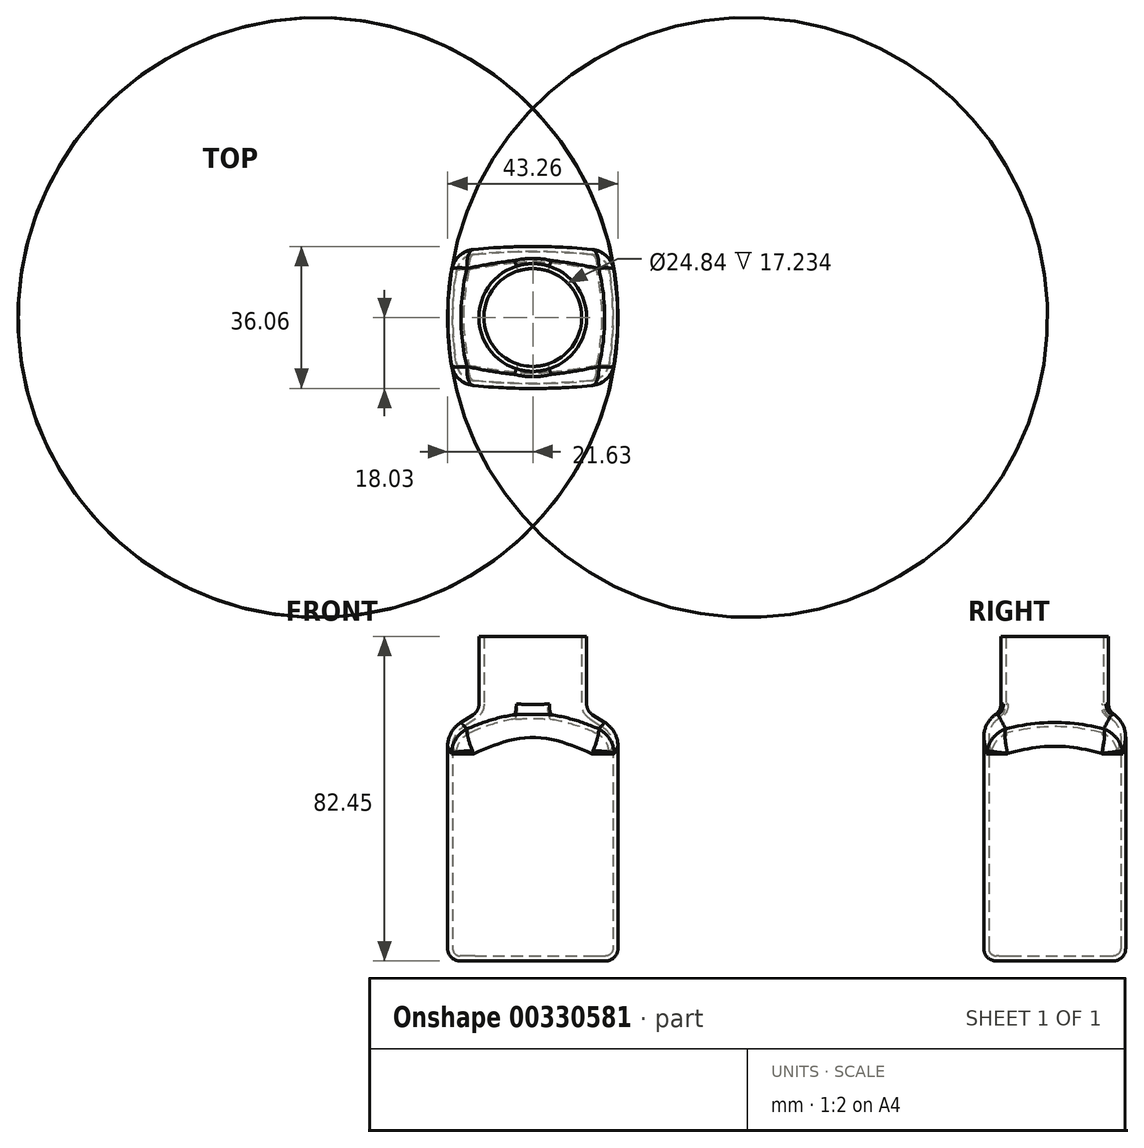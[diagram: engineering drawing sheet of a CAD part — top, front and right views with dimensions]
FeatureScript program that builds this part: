
annotation { "Feature Type Name" : "Feature", "Feature Type Description" : "" }
export const myFeature = defineFeature(function(context is Context, id is Id, definition is map)
    precondition{}
    {
        {
            var Q0;
            Q0=qCreatedBy(makeId("Top.planeOp"),FACE);
            var sketch = newSketch(context, id + "F0", { "sketchPlane" : qUnion([Q0])});
            skLineSegment(sketch, "E0.bottom", {"start": v(21.63, -18.03) * mm, "end": v(-21.63, -18.03) * mm, "construction": true});
            skLineSegment(sketch, "E0.top", {"start": v(21.63, 18.03) * mm, "end": v(-21.63, 18.03) * mm, "construction": true});
            skLineSegment(sketch, "E0.left", {"start": v(21.63, -18.03) * mm, "end": v(21.63, 18.03) * mm, "construction": true});
            skLineSegment(sketch, "E0.right", {"start": v(-21.63, -18.03) * mm, "end": v(-21.63, 18.03) * mm, "construction": true});
            skPoint(sketch, "E0.middle", {"position": v(0, 0) * mm});
            skLineSegment(sketch, "E1.0", {"start": v(21.63, -134.37) * mm, "end": v(-21.63, -134.37) * mm, "construction": true});
            skLineSegment(sketch, "E2.0", {"start": v(21.63, 134.37) * mm, "end": v(-21.63, 134.37) * mm, "construction": true});
            skLineSegment(sketch, "E3.0", {"start": v(-54.57, -18.03) * mm, "end": v(-54.57, 18.03) * mm, "construction": true});
            skLineSegment(sketch, "E4.0", {"start": v(54.57, -18.03) * mm, "end": v(54.57, 18.03) * mm, "construction": true});
            skArc(sketch, "E5", {"start": v(-15.04, -17.3) * mm, "mid": v(0, -18.03) * mm, "end": v(15.04, -17.3) * mm});
            skArc(sketch, "E6", {"start": v(20.68, -11.97) * mm, "mid": v(21.63, 0) * mm, "end": v(20.68, 11.97) * mm});
            skArc(sketch, "E7", {"start": v(-20.68, 11.97) * mm, "mid": v(-21.63, 0) * mm, "end": v(-20.68, -11.97) * mm});
            skArc(sketch, "E8.trimOffspring", {"start": v(15.04, 17.3) * mm, "mid": v(0, 18.03) * mm, "end": v(-15.04, 17.3) * mm});
            skPoint(sketch, "E9.visualSharp", {"position": v(-19.77, 16.75) * mm});
            skArc(sketch, "E9.filletArc", {"start": v(-15.04, 17.3) * mm, "mid": v(-18.77, 15.6) * mm, "end": v(-20.68, 11.97) * mm});
            skPoint(sketch, "E10.visualSharp", {"position": v(-19.77, -16.75) * mm});
            skArc(sketch, "E10.filletArc", {"start": v(-20.68, -11.97) * mm, "mid": v(-18.77, -15.6) * mm, "end": v(-15.04, -17.3) * mm});
            skPoint(sketch, "E11.visualSharp", {"position": v(19.77, -16.75) * mm});
            skArc(sketch, "E11.filletArc", {"start": v(15.04, -17.3) * mm, "mid": v(18.77, -15.6) * mm, "end": v(20.68, -11.97) * mm});
            skPoint(sketch, "E12.visualSharp", {"position": v(19.77, 16.75) * mm});
            skArc(sketch, "E12.filletArc", {"start": v(20.68, 11.97) * mm, "mid": v(18.77, 15.6) * mm, "end": v(15.04, 17.3) * mm});
            skSolve(sketch);
        }
        {
            var Q0;
            Q0 = qSketchRegion(id + "F0", true);
            extrude(context, id + "F1", {"entities" : qUnion([Q0]), "depth" : 82.45 * mm});
        }
        {
            var Q0;
            Q0=qCreatedBy(makeId("Front.planeOp"),FACE);
            var sketch = newSketch(context, id + "F2", { "sketchPlane" : qUnion([Q0])});
            skLineSegment(sketch, "E13", {"start": v(0, 0) * mm, "end": v(0, 82.45) * mm, "construction": true});
            skLineSegment(sketch, "E14.0", {"start": v(13.7, 63.48) * mm, "end": v(13.7, 82.45) * mm});
            skLineSegment(sketch, "E15", {"start": v(0, 82.45) * mm, "end": v(13.7, 82.45) * mm, "construction": true});
            skLineSegment(sketch, "E16", {"start": v(0, 0) * mm, "end": v(21.63, 0) * mm, "construction": true});
            skLineSegment(sketch, "E17.0", {"start": v(0, 54.56) * mm, "end": v(21.63, 54.56) * mm, "construction": true});
            skLineSegment(sketch, "E18", {"start": v(21.63, 0) * mm, "end": v(21.63, 54.56) * mm, "construction": true});
            skArc(sketch, "E19", {"start": v(21.63, 54.56) * mm, "mid": v(20.73, 58.02) * mm, "end": v(18.27, 60.61) * mm, "construction": true});
            skLineSegment(sketch, "E20", {"start": v(34.01, 50.78) * mm, "end": v(13.7, 63.48) * mm});
            skLineSegment(sketch, "E21", {"start": v(34.01, 82.45) * mm, "end": v(13.7, 82.45) * mm});
            skLineSegment(sketch, "E22", {"start": v(34.01, 50.78) * mm, "end": v(34.01, 82.45) * mm});
            skSolve(sketch);
        }
        {
            var Q0;
            Q0=makeQuery(id+"F2.imprint","IMPRINT",FACE,{"disambiguationData":[TD([[makeQuery(id+"F2.imprint","IMPRINT",EDGE,{"derivedFrom":sQuery(id+"F2.wireOp",EDGE,"E14.0")}),-1.0]])]});
            var Q1;
            Q1=sQuery(id+"F2.wireOp",EDGE,"E13");
            revolve(context, id + "F3", {"entities" : qUnion([Q0]), "axis" : qUnion([Q1]), "revolveType" : RevolveType.FULL});
        }
        {
            var Q0;
            Q0=makeQuery(id+"F3.opRevolve","SWEPT_BODY",BODY,{"disambiguationData":[OSD([sQuery(id+"F2.wireOp",EDGE,"E14.0"),sQuery(id+"F2.wireOp",EDGE,"E20"),sQuery(id+"F2.wireOp",EDGE,"E21"),sQuery(id+"F2.wireOp",EDGE,"E22")])]});
            var Q1;
            Q1=makeQuery(id+"F1.opExtrude","SWEPT_BODY",BODY,{"disambiguationData":[OSD([sQuery(id+"F0.wireOp",EDGE,"E5"),sQuery(id+"F0.wireOp",EDGE,"E6"),sQuery(id+"F0.wireOp",EDGE,"E7"),sQuery(id+"F0.wireOp",EDGE,"E8.trimOffspring"),sQuery(id+"F0.wireOp",EDGE,"E9.filletArc"),sQuery(id+"F0.wireOp",EDGE,"E10.filletArc"),sQuery(id+"F0.wireOp",EDGE,"E11.filletArc"),sQuery(id+"F0.wireOp",EDGE,"E12.filletArc")])]});
            booleanBodies(context, id + "F4", {"operationType" : BooleanOperationType.SUBTRACTION, "tools" : qUnion([Q0]), "targets" : qUnion([Q1])});
        }
        {
            var Q0;
            Q0=makeQuery(id+"F4.opBoolean","INTERSECT",EDGE,{"derivedFrom":[makeQuery(id+"F1.opExtrude","SWEPT_FACE",FACE,{"disambiguationData":[OSD([sQuery(id+"F0.wireOp",EDGE,"E11.filletArc")])]}),makeQuery(id+"F3.opRevolve","SWEPT_FACE",FACE,{"disambiguationData":[OSD([sQuery(id+"F2.wireOp",EDGE,"E20")])]})]});
            var Q1;
            Q1=makeQuery(id+"F4.opBoolean","INTERSECT",EDGE,{"derivedFrom":[makeQuery(id+"F1.opExtrude","SWEPT_FACE",FACE,{"disambiguationData":[OSD([sQuery(id+"F0.wireOp",EDGE,"E6")])]}),makeQuery(id+"F3.opRevolve","SWEPT_FACE",FACE,{"disambiguationData":[OSD([sQuery(id+"F2.wireOp",EDGE,"E20")])]})]});
            fillet(context, id + "F5", {"entities" : qUnion([Q0, Q1]), "radius" : 7.14 * mm, "tangentPropagation" : true, "allowEdgeOverflow" : false});
        }
        {
            var Q0;
            Q0=makeQuery(id+"F1.opExtrude","CAP_FACE",FACE,{"disambiguationData":[OSD([sQuery(id+"F0.wireOp",EDGE,"E5"),sQuery(id+"F0.wireOp",EDGE,"E6"),sQuery(id+"F0.wireOp",EDGE,"E7"),sQuery(id+"F0.wireOp",EDGE,"E8.trimOffspring"),sQuery(id+"F0.wireOp",EDGE,"E9.filletArc"),sQuery(id+"F0.wireOp",EDGE,"E10.filletArc"),sQuery(id+"F0.wireOp",EDGE,"E11.filletArc"),sQuery(id+"F0.wireOp",EDGE,"E12.filletArc")])],"isStart":true});
            fillet(context, id + "F6", {"entities" : qUnion([Q0]), "radius" : 3.17 * mm, "tangentPropagation" : true, "allowEdgeOverflow" : false});
        }
        {
            var Q0;
            Q0=makeQuery(id+"F4.opBoolean","COPY",FACE,{"derivedFrom":makeQuery(id+"F3.opRevolve","SWEPT_FACE",FACE,{"disambiguationData":[OSD([sQuery(id+"F2.wireOp",EDGE,"E20")])]})});
            fillet(context, id + "F7", {"entities" : qUnion([Q0]), "radius" : 3.17 * mm, "tangentPropagation" : true, "allowEdgeOverflow" : false});
        }
        {
            var Q0;
            Q0=makeQuery(id+"F1.opExtrude","CAP_FACE",FACE,{"disambiguationData":[OSD([sQuery(id+"F0.wireOp",EDGE,"E5"),sQuery(id+"F0.wireOp",EDGE,"E6"),sQuery(id+"F0.wireOp",EDGE,"E7"),sQuery(id+"F0.wireOp",EDGE,"E8.trimOffspring"),sQuery(id+"F0.wireOp",EDGE,"E9.filletArc"),sQuery(id+"F0.wireOp",EDGE,"E10.filletArc"),sQuery(id+"F0.wireOp",EDGE,"E11.filletArc"),sQuery(id+"F0.wireOp",EDGE,"E12.filletArc")])],"isStart":false});
            shell(context, id + "F8", {"entities" : qUnion([Q0]), "thickness" : 1.27 * mm});
        }
    });
